# Revit family: Halter 45- 26-52 l-q
name_source: partatom
category: HLS-Bauteile
revit_build: Autodesk Revit 2017 (Build: 20190507_1515(x64)
units: mm (PartAtom-declared; Revit-internal decimal feet)

## family parameters
Basisbauteil = Fläche
Beim Laden mit Abzugskörper schneiden = Nein
Bemaßung runder Anschluss = Durchmesser verwenden
Gemeinsam genutzt = Ja
Raumberechnungspunkt = Nein
Teiletyp = Normal

## types (2) — shared parameters
Ausrichtung Platte = längs / quer
Befestigung = am Baukörper, die notwendigen Dübellöcher sind wie das x im Bild zu setzen
Breite Platte = 100 mm  [stored 0.328084 ft]
Fabrikat = MEFA
Firma = MEFA Befestigungs- und Montagesysteme GmbH
Kurztext1 = Halter C-Profil 45 längs / quer
Langloch = val.Langloch.14x20 mm
Lochabstand = 88 mm
Lochdurchmesser = 14 mm
Länge Platte = 100 mm  [stored 0.328084 ft]
Material = Stahl
Mengeneinheit = St
Profil = C-Profil
Profilname = 45/26 - 45/52
Profiltyp = 45/26 - 45/52
Stärke Platte = 6 mm  [stored 0.019685 ft]
Vorgabe-Ansicht = 1219 mm
max. Profilhöhe = 52 mm
max. zul. Last Druck = 0.00 kip
zero-valued in all types: Länge, Sicherheitsfaktor

## per-type parameters (varying)
| type | Artikelnummer | EAN | Gewicht | Gewicht pro Bauteil | Kurztext2 |
| Halter 45- 26-52 l/q, gvz | 0812001 | 4250928459244 | 0.72 kg | 0.72 kg | für C-Profil 45/26 - 45/52 gvz |
| Halter 45- 26-52 l/q, fvz | 0812002 | 4250928459251 | 0.75 kg | 0.75 kg | für C-Profil 45/26 - 45/52 fsv |

note: [stored X ft] marks values corroborated as IEEE doubles in the binary element streams (Revit-internal decimal feet)
